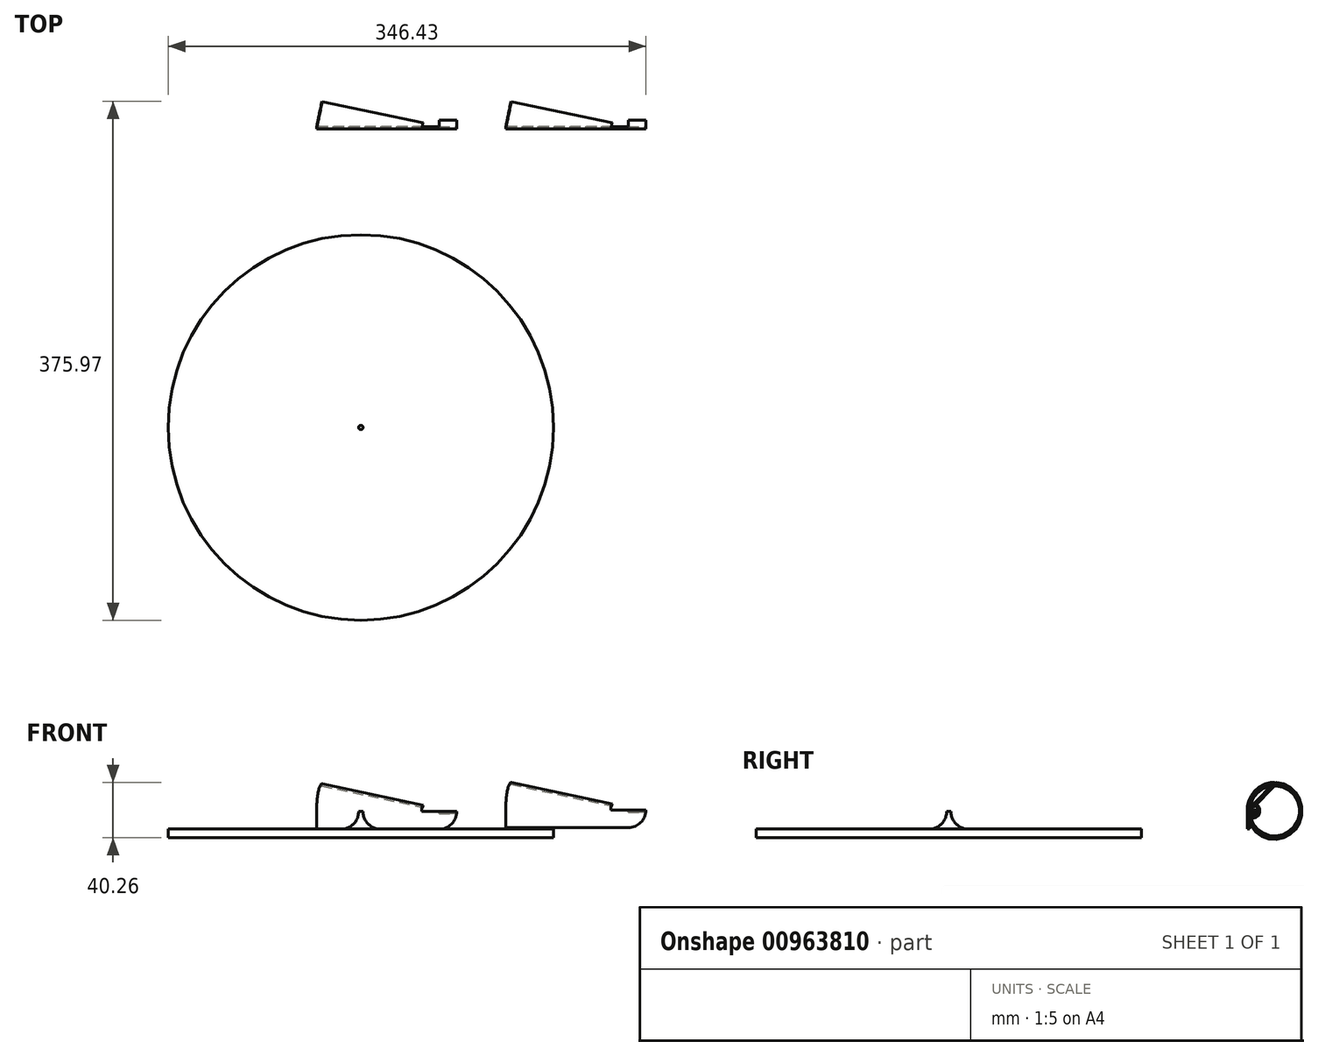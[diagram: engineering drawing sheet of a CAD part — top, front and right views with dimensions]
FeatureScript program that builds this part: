
annotation { "Feature Type Name" : "Feature", "Feature Type Description" : "" }
export const myFeature = defineFeature(function(context is Context, id is Id, definition is map)
    precondition{}
    {
        {
            var Q0;
            Q0=qCreatedBy(makeId("Front.planeOp"),FACE);
            var sketch = newSketch(context, id + "F0", { "sketchPlane" : qUnion([Q0])});
            skLineSegment(sketch, "E0", {"start": v(-1.55, 0) * mm, "end": v(-90.45, 0) * mm});
            skLineSegment(sketch, "E1", {"start": v(-90.45, 0) * mm, "end": v(-90.45, 12.7) * mm});
            skLineSegment(sketch, "E2", {"start": v(-90.45, 12.7) * mm, "end": v(11.15, 12.7) * mm});
            skArc(sketch, "E3", {"start": v(-1.55, 0) * mm, "mid": v(7.43, 3.72) * mm, "end": v(11.15, 12.7) * mm});
            skSolve(sketch);
        }
        {
            var Q0;
            Q0=makeQuery(id+"F0.imprint","IMPRINT",FACE,{"disambiguationData":[TD([[makeQuery(id+"F0.imprint","IMPRINT",EDGE,{"derivedFrom":sQuery(id+"F0.wireOp",EDGE,"E0")}),-1.0]])]});
            extrude(context, id + "F1", {"entities" : qUnion([Q0]), "depth" : 1.57 * mm, "offsetDistance" : 25.4 * mm});
        }
        {
            var Q0;
            Q0=makeQuery(id+"F1.opExtrude","SWEPT_FACE",FACE,{"disambiguationData":[OSD([sQuery(id+"F0.wireOp",EDGE,"E2")])]});
            var sketch = newSketch(context, id + "F2", { "sketchPlane" : qUnion([Q0])});
            skLineSegment(sketch, "E4.bottom", {"start": v(11.15, -1.57) * mm, "end": v(-1.55, -1.57) * mm});
            skLineSegment(sketch, "E4.top", {"start": v(11.15, 4.78) * mm, "end": v(-1.55, 4.78) * mm});
            skLineSegment(sketch, "E4.left", {"start": v(11.15, -1.57) * mm, "end": v(11.15, 4.78) * mm});
            skLineSegment(sketch, "E4.right", {"start": v(-1.55, -1.57) * mm, "end": v(-1.55, 4.78) * mm});
            skSolve(sketch);
        }
        {
            var Q0;
            {var subQ0=sQuery(id+"F2.wireOp",EDGE,"E4.top");Q0=makeQuery(id+"F2.imprint","IMPRINT",FACE,{"disambiguationData":[TD([[makeQuery(id+"F2.imprint","IMPRINT",EDGE,{"derivedFrom":subQ0}),1.0]])]});}
            extrude(context, id + "F3", {"entities" : qUnion([Q0]), "operationType" : NewBodyOperationType.ADD, "oppositeDirection" : true, "depth" : 1.57 * mm, "offsetDistance" : 25.4 * mm});
        }
        {
            var Q0;
            {var subQ0=sQuery(id+"F0.wireOp",EDGE,"E2");Q0=makeQuery(id+"F3.boolean.opBoolean","MERGE",FACE,{"derivedFrom":[makeQuery(id+"F1.opExtrude","SWEPT_FACE",FACE,{"disambiguationData":[OSD([subQ0])]}),makeQuery(id+"F3.opExtrude","CAP_FACE",FACE,{"disambiguationData":[OSD([subQ0,sQuery(id+"F2.wireOp",EDGE,"E4.top"),sQuery(id+"F2.wireOp",EDGE,"E4.left"),sQuery(id+"F2.wireOp",EDGE,"E4.right")])],"isStart":true})]});}
            var sketch = newSketch(context, id + "F4", { "sketchPlane" : qUnion([Q0])});
            skLineSegment(sketch, "E5", {"start": v(-90.45, -1.57) * mm, "end": v(-14.25, -1.57) * mm});
            skLineSegment(sketch, "E6", {"start": v(-14.25, -1.57) * mm, "end": v(-14.25, 0) * mm});
            skLineSegment(sketch, "E7", {"start": v(-14.25, 0) * mm, "end": v(-90.45, 0) * mm});
            skLineSegment(sketch, "E8", {"start": v(-90.45, 0) * mm, "end": v(-90.45, -1.57) * mm});
            skLineSegment(sketch, "E9", {"start": v(-14.25, 0) * mm, "end": v(-14.25, 3.18) * mm, "construction": true});
            skLineSegment(sketch, "E10", {"start": v(-90.45, 0) * mm, "end": v(-90.45, 19.05) * mm, "construction": true});
            skLineSegment(sketch, "E11", {"start": v(-90.45, 19.05) * mm, "end": v(-14.25, 3.18) * mm, "construction": true});
            skSolve(sketch);
        }
        {
            var Q0;
            Q0=makeQuery(id+"F4.imprint","IMPRINT",FACE,{"disambiguationData":[TD([[makeQuery(id+"F4.imprint","IMPRINT",EDGE,{"derivedFrom":sQuery(id+"F4.wireOp",EDGE,"E5")}),1.0]])]});
            var Q1;
            Q1=sQuery(id+"F4.wireOp",EDGE,"E11");
            revolve(context, id + "F5", {"operationType" : NewBodyOperationType.ADD, "surfaceOperationType" : NewSurfaceOperationType.NEW, "entities" : qUnion([Q0]), "axis" : qUnion([Q1]), "revolveType" : RevolveType.ONE_DIRECTION, "oppositeDirection" : true, "angle" : 90 * degree});
        }
        {
            var Q0;
            Q0=makeQuery(id+"F1.opExtrude","SWEPT_BODY",BODY,{"disambiguationData":[OSD([sQuery(id+"F0.wireOp",EDGE,"E0"),sQuery(id+"F0.wireOp",EDGE,"E1"),sQuery(id+"F0.wireOp",EDGE,"E2"),sQuery(id+"F0.wireOp",EDGE,"E3")])]});
            transform(context, id + "F6", {"entities" : qUnion([Q0]), "transformType" : TransformType.TRANSLATION_3D, "dx" : 137.16 * mm, "dy" : 0 * mm, "dz" : 1.02 * mm, "makeCopy" : true});
        }
        {
            var Q0;
            Q0=qCreatedBy(makeId("Top.planeOp"),FACE);
            var sketch = newSketch(context, id + "F7", { "sketchPlane" : qUnion([Q0])});
            skCircle(sketch, "E12", {"center": v(-58.42, -218.01) * mm, "radius": 139.7 * mm});
            skSolve(sketch);
        }
        {
            var Q0;
            Q0=makeQuery(id+"F7.imprint","IMPRINT",FACE,{"disambiguationData":[TD([[makeQuery(id+"F7.imprint","IMPRINT",EDGE,{"derivedFrom":sQuery(id+"F7.wireOp",EDGE,"E12")}),1.0]])]});
            extrude(context, id + "F8", {"entities" : qUnion([Q0]), "oppositeDirection" : true, "depth" : 6.35 * mm, "offsetDistance" : 25.4 * mm});
        }
        {
            var Q0;
            Q0=makeQuery(id+"F8.opExtrude","CAP_EDGE",EDGE,{"disambiguationData":[OSD([sQuery(id+"F7.wireOp",EDGE,"E12")])],"isStart":true});
            cPlane(context, id + "F9", {"entities" : qUnion([Q0]), "cplaneType" : CPlaneType.LINE_ANGLE, "offset" : 25.4 * mm, "angle" : 0 * degree, "width" : 152.4 * mm, "height" : 152.4 * mm});
        }
        {
            var Q0;
            Q0=qCreatedBy(id+"F9.planeOp",FACE);
            var sketch = newSketch(context, id + "F10", { "sketchPlane" : qUnion([Q0])});
            skPoint(sketch, "E13", {"position": v(-218.01, 0) * mm});
            skLineSegment(sketch, "E14", {"start": v(-218.01, 0) * mm, "end": v(-218.01, 12.7) * mm});
            skLineSegment(sketch, "E15.0", {"start": v(-216.42, 0) * mm, "end": v(-216.42, 12.7) * mm, "construction": true});
            skLineSegment(sketch, "E16", {"start": v(-216.42, 12.7) * mm, "end": v(-218.01, 12.7) * mm});
            skLineSegment(sketch, "E17", {"start": v(-216.42, 12.7) * mm, "end": v(-203.72, 12.7) * mm, "construction": true});
            skLineSegment(sketch, "E18", {"start": v(-203.72, 12.7) * mm, "end": v(-203.72, 0) * mm, "construction": true});
            skArc(sketch, "E19", {"start": v(-216.42, 12.7) * mm, "mid": v(-212.7, 3.72) * mm, "end": v(-203.72, 0) * mm});
            skLineSegment(sketch, "E20", {"start": v(-203.72, 0) * mm, "end": v(-218.01, 0) * mm});
            skSolve(sketch);
        }
        {
            var Q0;
            Q0=makeQuery(id+"F10.imprint","IMPRINT",FACE,{"disambiguationData":[TD([[makeQuery(id+"F10.imprint","IMPRINT",EDGE,{"derivedFrom":sQuery(id+"F10.wireOp",EDGE,"E14")}),-1.0]])]});
            var Q1;
            Q1=sQuery(id+"F10.wireOp",EDGE,"E14");
            revolve(context, id + "F11", {"operationType" : NewBodyOperationType.ADD, "surfaceOperationType" : NewSurfaceOperationType.NEW, "entities" : qUnion([Q0]), "axis" : qUnion([Q1]), "revolveType" : RevolveType.FULL});
        }
    });
